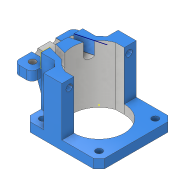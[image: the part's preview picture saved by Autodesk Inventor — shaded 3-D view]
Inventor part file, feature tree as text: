
AUTODESK INVENTOR PART (.ipt)
format: ipt  version: 2020 (Build 240168000, 168)  size: 436,224 bytes
history: native  units: in
note: dims shown in document units (in); Inventor stores cm internally (conversion verified against a paired STEP export)
features: sketch x26, extrude x20, mirror x11, thicken_offset x4, plane x2, sweep x2, chamfer x2, pattern_linear x1, fillet x1
ambient origin geometry x8: Origin, YZ Plane, XZ Plane, XY Plane, X Axis, Y Axis, Z Axis, Center Point
bodies: Solid1 (feature_tree)
feature tree (69):
  extrude  "Extrusion1"  Depth=1.6142in
  extrude  "Extrusion2"  Depth=0.1969in
  extrude  "Extrusion3"  Depth=0.1969in
  pattern_linear  "Rectangular Pattern1"  Count1=2 Spacing1=1.2205in
  extrude  "Extrusion4"  Depth=0.7874in
  extrude  "Extrusion5"  Depth=1.2598in TaperAngle=0.0deg
  extrude  "Extrusion6"  Depth=0.3937in
  plane  "Work Plane1"
  mirror  "Mirror1"
  extrude  "Extrusion7"  [1 undecoded]
  extrude  "Extrusion8"  Depth=1.2598in TaperAngle=0.0deg
  mirror  "Mirror2"
  sketch  "Sketch10"  dims[d28=0.9055in d29=1.2598in d30=0.0in]
  sketch  "Sketch11"  dims[d31=165.0deg d35=0.2756in d36=0.0in]
  sweep  "Sweep1"
  mirror  "Mirror3"
  extrude  "Extrusion9"  Depth=0.9055in
  extrude  "Extrusion10"  Depth=0.3937in TaperAngle=0.0deg
  extrude  "Extrusion11"  Depth=0.1969in TaperAngle=0.0deg
  mirror  "Mirror4"
  extrude  "Extrusion12"  Depth=0.1969in TaperAngle=0.0deg
  mirror  "Mirror5"
  extrude  "Extrusion14"  Depth=0.3937in
  mirror  "Mirror6"
  extrude  "Extrusion15"  Depth=0.9843in
  chamfer  "Chamfer1"  Distance=0.9843in
  fillet  "Fillet1"  Radius=0.0984in
  extrude  "Extrusion16"  Depth=0.1969in
  mirror  "Mirror7"
  extrude  "Extrusion17"  Depth=0.1969in
  mirror  "Mirror8"
  chamfer  "Chamfer2"  Distance=0.1969in
  thicken_offset  "Thicken1"
  thicken_offset  "Thicken2"
  thicken_offset  "Thicken3"
  extrude  "Extrusion18"  Depth=0.0315in
  plane  "Work Plane2"
  sketch  "Sketch23"  dims[d74=0.1969in d75=0.1969in]
  sketch  "Sketch24"  dims[d76=0.1969in]
  sweep  "Sweep2"
  mirror  "Mirror9"
  extrude  "Extrusion19"  TaperAngle=0.0deg  [1 undecoded]
  mirror  "Mirror10"
  extrude  "Extrusion20"  Depth=0.3937in TaperAngle=0.0deg
  extrude  "Extrusion21"  Depth=1.158in
  mirror  "Mirror11"
  thicken_offset  "Thicken4"
  sketch  "Sketch1"  dims[d0=1.6142in d1=1.6142in]
  sketch  "Sketch2"  dims[d2=0.1969in d3=0.0in d4=0.5906in]
  sketch  "Sketch3"  dims[d5=0.1969in d6=0.0in d7=0.1417in]
  sketch  "Sketch4"  dims[d8=0.1969in d9=0.0in d10=0.7874in d12=1.2205in]
  sketch  "Sketch5"  dims[d13=0.7874in d15=1.2205in d16=0.9567in]
  sketch  "Sketch6"  dims[d17=1.378in d18=1.2598in d19=0.0in]
  sketch  "Sketch8"  dims[d20=1.2598in d21=0.0in d22=0.3937in]
  sketch  "Sketch9"  dims[d23=1.2598in d24=0.0in d25=-0.8071in]
  sketch  "3D Sketch1"
  sketch  "Sketch12"  dims[d37=0.0in d38=0.0in d39=0.9055in]
  sketch  "Sketch13"  dims[d40=0.1969in d41=0.3937in d42=0.0in]
  sketch  "Sketch14"  dims[d43=0.3937in d44=0.0in d45=0.1969in d46=0.0in]
  sketch  "Sketch15"  dims[d48=0.1969in d49=0.0in d54=0.0984in d55=0.0in]
  sketch  "Sketch18"  dims[d56=0.3937in d57=0.4724in]
  sketch  "Sketch19"  dims[d58=0.9843in d59=0.0in d60=0.3543in d61=0.0787in d62=0.481in]
  sketch  "Sketch20"  dims[d63=0.1181in]
  sketch  "Sketch21"  dims[d64=0.1417in d65=0.9843in d66=0.0in d68=0.0984in d69=0.0in]
  sketch  "Sketch22"  dims[d70=0.1181in d71=0.0787in d72=0.481in d73=0.1969in]
  sketch  "3D Sketch2"
  sketch  "Sketch25"  dims[d77=0.1969in]
  sketch  "Sketch26"  dims[d78=0.1969in d79=0.1969in d80=0.0in]
  sketch  "Sketch27"  dims[d81=0.1417in d84=0.126in d85=0.0in d86=0.0in d87=0.0in d88=0.3937in d89=0.0in d90=1.158in d91=1.5748in d92=0.0in d93=0.2756in d94=0.0315in d95=0.3937in d96=0.0in d97=0.0315in d98=0.0315in d99=0.0984in d100=0.0in]
note: 2 required parameter values undecoded (feature->parameter linkage not recoverable at this tier; creation-order binding heuristic only, values carry confidence <= 0.55)
